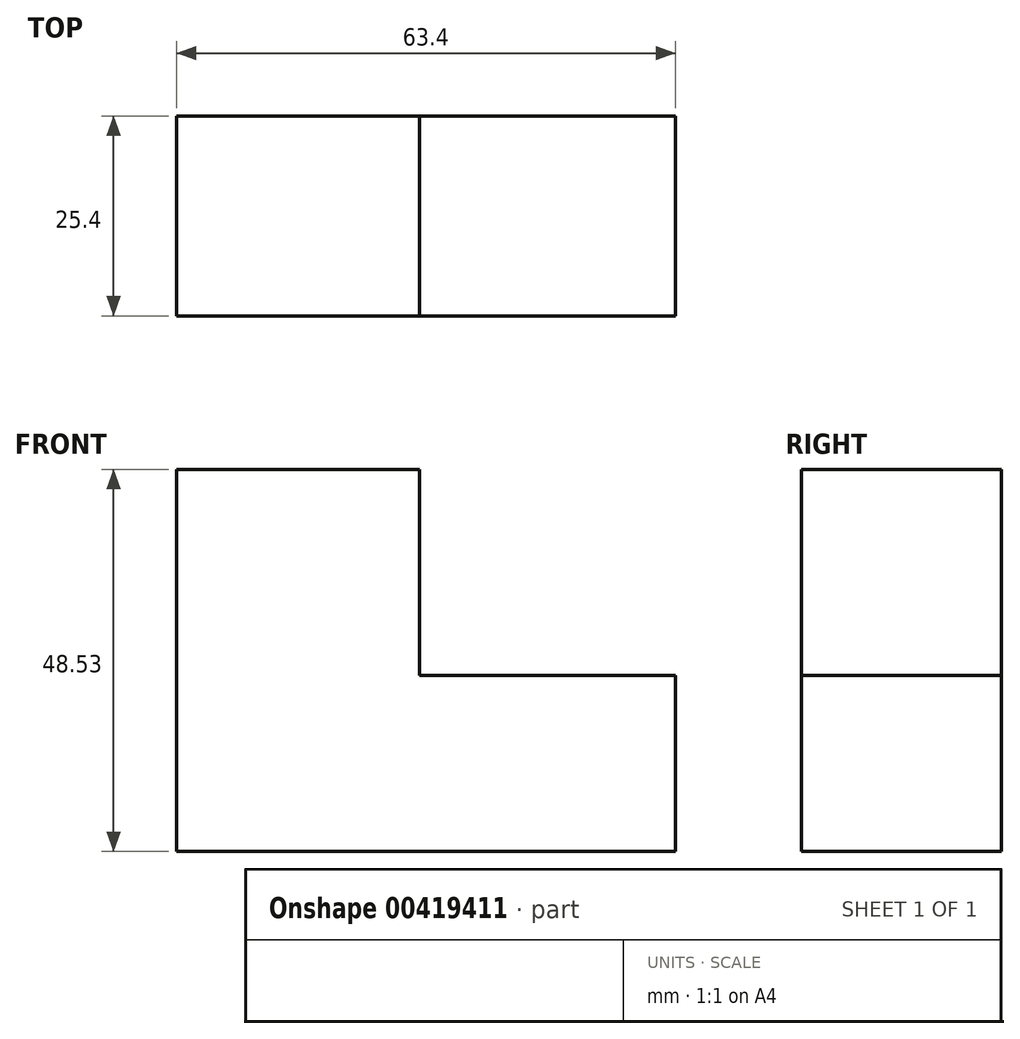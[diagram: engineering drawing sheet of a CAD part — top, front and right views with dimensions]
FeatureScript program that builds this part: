
annotation { "Feature Type Name" : "Feature", "Feature Type Description" : "" }
export const myFeature = defineFeature(function(context is Context, id is Id, definition is map)
    precondition{}
    {
        {
            var Q0;
            Q0=qCreatedBy(makeId("Front.planeOp"),FACE);
            var sketch = newSketch(context, id + "F0", { "sketchPlane" : qUnion([Q0])});
            skLineSegment(sketch, "E0", {"start": v(0, 0) * mm, "end": v(-63.4, 0) * mm});
            skLineSegment(sketch, "E1", {"start": v(-63.4, 0) * mm, "end": v(-63.4, 48.53) * mm});
            skLineSegment(sketch, "E2", {"start": v(-63.4, 48.53) * mm, "end": v(-32.53, 48.53) * mm});
            skLineSegment(sketch, "E3", {"start": v(-32.53, 48.53) * mm, "end": v(-32.53, 22.36) * mm});
            skLineSegment(sketch, "E4", {"start": v(-32.53, 22.36) * mm, "end": v(0, 22.36) * mm});
            skLineSegment(sketch, "E5", {"start": v(0, 22.36) * mm, "end": v(0, 0) * mm});
            skSolve(sketch);
        }
        {
            var Q0;
            Q0=makeQuery(id+"F0.imprint","IMPRINT",FACE,{"disambiguationData":[TD([[makeQuery(id+"F0.imprint","IMPRINT",EDGE,{"derivedFrom":sQuery(id+"F0.wireOp",EDGE,"E0")}),-1.0]])]});
            extrude(context, id + "F1", {"entities" : qUnion([Q0]), "depth" : 25.4 * mm});
        }
    });
